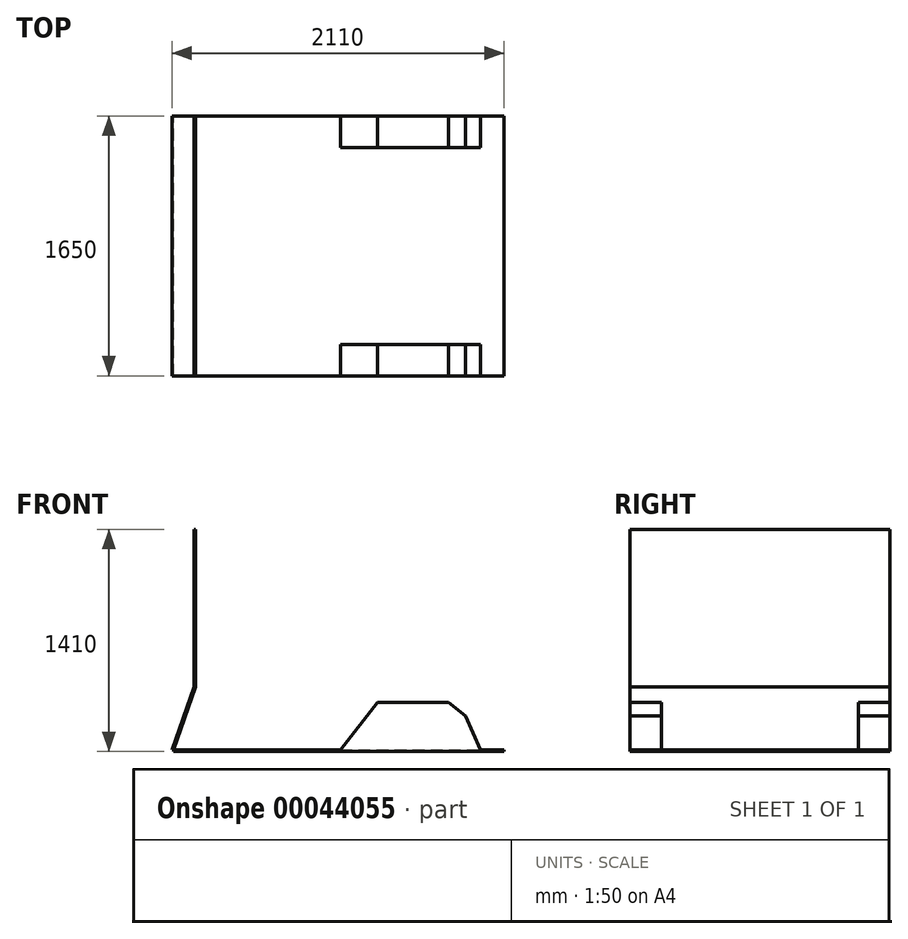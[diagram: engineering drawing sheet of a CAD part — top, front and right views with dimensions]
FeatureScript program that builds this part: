
annotation { "Feature Type Name" : "Feature", "Feature Type Description" : "" }
export const myFeature = defineFeature(function(context is Context, id is Id, definition is map)
    precondition{}
    {
        {
            var Q0;
            Q0=qCreatedBy(makeId("Top.planeOp"),FACE);
            var sketch = newSketch(context, id + "F0", { "sketchPlane" : qUnion([Q0])});
            skLineSegment(sketch, "E0.bottom", {"start": v(0, 0) * mm, "end": v(2100, 0) * mm});
            skLineSegment(sketch, "E0.top", {"start": v(0, 1650) * mm, "end": v(2100, 1650) * mm});
            skLineSegment(sketch, "E0.left", {"start": v(0, 0) * mm, "end": v(0, 1650) * mm});
            skLineSegment(sketch, "E0.right", {"start": v(2100, 0) * mm, "end": v(2100, 1650) * mm});
            skSolve(sketch);
        }
        {
            var Q0;
            Q0=qCreatedBy(makeId("Front.planeOp"),FACE);
            var sketch = newSketch(context, id + "F1", { "sketchPlane" : qUnion([Q0])});
            skLineSegment(sketch, "E1", {"start": v(0, 0) * mm, "end": v(140, 400) * mm});
            skLineSegment(sketch, "E2", {"start": v(140, 400) * mm, "end": v(140, 1400) * mm});
            skLineSegment(sketch, "E3", {"start": v(140, 1400) * mm, "end": v(130, 1400) * mm});
            skLineSegment(sketch, "E4", {"start": v(130, 1400) * mm, "end": v(130, 400) * mm});
            skLineSegment(sketch, "E5", {"start": v(130, 400) * mm, "end": v(-10, 0) * mm});
            skLineSegment(sketch, "E6", {"start": v(-10, 0) * mm, "end": v(0, 0) * mm});
            skSolve(sketch);
        }
        {
            var Q0;
            Q0 = qSketchRegion(id + "F0", true);
            extrude(context, id + "F2", {"entities" : qUnion([Q0]), "oppositeDirection" : true, "depth" : 10 * mm});
        }
        {
            var Q0;
            Q0 = qSketchRegion(id + "F1", true);
            extrude(context, id + "F3", {"entities" : qUnion([Q0]), "oppositeDirection" : true, "depth" : 1650 * mm});
        }
        {
            var Q0;
            Q0=makeQuery(id+"F2.opExtrude","SWEPT_FACE",FACE,{"disambiguationData":[OSD([sQuery(id+"F0.wireOp",EDGE,"E0.bottom")])]});
            var sketch = newSketch(context, id + "F4", { "sketchPlane" : qUnion([Q0])});
            skLineSegment(sketch, "E7", {"start": v(1950, 0) * mm, "end": v(1855.37, 214.27) * mm});
            skLineSegment(sketch, "E8", {"start": v(1855.37, 214.27) * mm, "end": v(1747.18, 300) * mm});
            skLineSegment(sketch, "E9", {"start": v(1747.18, 300) * mm, "end": v(1297.18, 300) * mm});
            skLineSegment(sketch, "E10", {"start": v(1297.18, 300) * mm, "end": v(1060, 0) * mm});
            skLineSegment(sketch, "E11", {"start": v(1060, 0) * mm, "end": v(1950, 0) * mm});
            skSolve(sketch);
        }
        {
            var Q0;
            Q0 = qSketchRegion(id + "F4", true);
            extrude(context, id + "F5", {"entities" : qUnion([Q0]), "operationType" : NewBodyOperationType.ADD, "oppositeDirection" : true, "depth" : 200 * mm});
        }
        {
            var Q0;
            Q0=makeQuery(id+"F2.opExtrude","SWEPT_FACE",FACE,{"disambiguationData":[OSD([sQuery(id+"F0.wireOp",EDGE,"E0.top")])]});
            var sketch = newSketch(context, id + "F6", { "sketchPlane" : qUnion([Q0])});
            skLineSegment(sketch, "E12.0.0", {"start": v(-1950, 0) * mm, "end": v(-1060, 0) * mm});
            skLineSegment(sketch, "E12.0.1", {"start": v(-1060, 0) * mm, "end": v(-1297.18, 300) * mm});
            skLineSegment(sketch, "E12.0.2", {"start": v(-1297.18, 300) * mm, "end": v(-1747.18, 300) * mm});
            skLineSegment(sketch, "E12.0.3", {"start": v(-1747.18, 300) * mm, "end": v(-1855.37, 214.27) * mm});
            skLineSegment(sketch, "E12.0.4", {"start": v(-1855.37, 214.27) * mm, "end": v(-1950, 0) * mm});
            skSolve(sketch);
        }
        {
            var Q0;
            Q0 = qSketchRegion(id + "F6", true);
            extrude(context, id + "F7", {"entities" : qUnion([Q0]), "operationType" : NewBodyOperationType.ADD, "oppositeDirection" : true, "depth" : 200 * mm});
        }
    });
